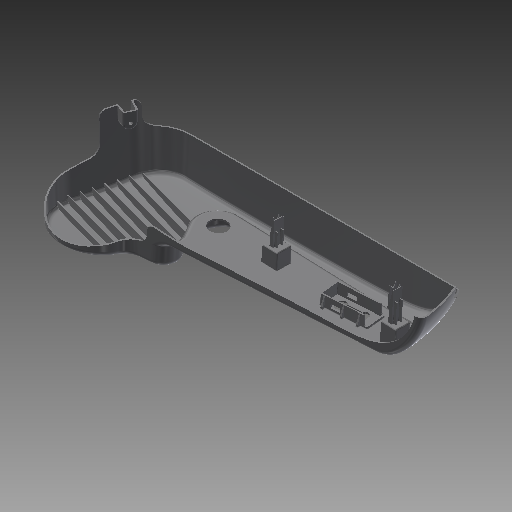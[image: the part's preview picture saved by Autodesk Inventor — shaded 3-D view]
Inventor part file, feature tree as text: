
AUTODESK INVENTOR PART (.ipt)
format: ipt  version: 2019 (Build 230136000, 136)  size: 7,566,848 bytes
history: native  units: in
note: dims shown in document units (in); Inventor stores cm internally (conversion verified against a paired STEP export)
features: other x32, fillet x25, surface_op x15, sketch x14, extrude x9, plane x8, split x7, delete_face x3, rib x3, projected_geometry x2, thicken_offset x1, draft x1, reference x1, loft x1
ambient origin geometry x8: Origin, YZ Plane, XZ Plane, XY Plane, X Axis, Y Axis, Z Axis, Center Point
bodies: Solid1 (feature_tree)
feature tree (122):
  surface_op  "Extend1"
  surface_op  "Extend2"
  surface_op  "Stitch Surface1"
  plane  "Work Plane1"
  surface_op  "Stitch Surface2"
  fillet  "Fillet1"  Radius=0.0787in
  split  "Split1"
  split  "Split2"
  split  "Split3"
  delete_face  "Delete Face1"
  plane  "Work Plane2"
  split  "Split4"
  split  "Split5"
  delete_face  "Delete Face2"
  split  "Split6"
  delete_face  "Delete Face3"
  thicken_offset  "Thicken1"
  fillet  "Fillet2"  Radius=0.0787in
  fillet  "Fillet3"  Radius=0.1969in
  extrude  "Extrusion1"  Depth=3.937in
  sketch  "Sketch6"  dims[d28=1.063in d29=9.0551in d30=0.0394in d31=0.0787in d32=0.0394in d33=0.0787in d34=0.0394in d35=-3.5433in]
  other  "iFeature3:1"
  other  "Work Point1"
  other  "Work Point2"
  other  "Work Point3"
  other  "iFeature8:2"
  fillet  "Fillet4"  Radius=0.7874in
  fillet  "Fillet5"  Radius=0.7874in
  other  "Work Point4"
  other  "Work Point5"
  other  "Work Point6"
  other  "iFeature8:3"
  fillet  "Fillet6"  [1 undecoded]
  fillet  "Fillet7"  Radius=4.9213in
  fillet  "Fillet8"  Radius=10.5in
  plane  "Work Plane3"
  other  "Work Axis1"
  sketch  "Sketch12"  dims[d47=0.0in d48=0.0in d83=0.7874in d84=0.2165in d85=0.0984in d86=0.0in d87=1.9685in d88=0.0in d89=0.0984in d98=0.0984in]
  extrude  "Extrusion4"  Depth=2.7559in
  extrude  "Extrusion5"  Depth=0.5906in
  plane  "Work Plane4"
  extrude  "Extrusion8"  [1 undecoded]
  plane  "Work Plane6"
  split  "Split8"
  draft  "FaceDraft1"
  extrude  "Extrusion9"  Depth=13.7795in
  fillet  "Fillet23"  Radius=0.0984in
  fillet  "Fillet24"  Radius=0.3937in
  fillet  "Fillet25"  Radius=0.3937in
  fillet  "Fillet26"  Radius=1.1811in
  plane  "Work Plane7"
  rib  "Rib3"
  fillet  "Fillet27"  Radius=0.3937in
  plane  "Work Plane8"
  plane  "Work Plane9"
  rib  "Rib4"
  extrude  "Extrusion10"  Depth=9.0551in
  fillet  "Fillet28"  Radius=0.0394in
  fillet  "Fillet29"  Radius=0.0787in
  fillet  "Fillet30"  Radius=0.0394in
  fillet  "Fillet31"  Radius=0.0787in
  fillet  "Fillet32"  Radius=0.0394in
  fillet  "Fillet33"  [1 undecoded]
  rib  "Rib5"
  extrude  "Extrusion11"  TaperAngle=0.0deg  [1 undecoded]
  fillet  "Fillet34"  Radius=0.7874in
  fillet  "Fillet35"  Radius=0.2165in
  fillet  "Fillet36"  Radius=0.0984in
  fillet  "Fillet37"  Radius=1.9685in
  fillet  "Fillet38"  Radius=0.0984in
  fillet  "Fillet39"  Radius=0.0984in
  other  "Srf5"
  other  "Srf6"
  other  "Edges1"
  other  "Edges2"
  other  "Srf7"
  other  "Srf8"
  sketch  "Sketch1"  dims[d3=0.7874in d4=3.937in d5=0.7874in d6=90.0deg d7=0.7874in d8=90.0deg d9=-13.7795in d10=4.9213in d11=10.5in d12=0.0in]
  other  "Srf9"
  sketch  "Sketch2"  dims[d13=0.7874in d14=2.7559in]
  other  "Srf12"
  other  "Srf13"
  sketch  "Sketch3"  dims[d15=2.5591in d16=0.5906in]
  other  "Srf14"
  sketch  "Sketch4"  dims[d17=26.5in d18=0.0in d19=-0.9843in]
  sketch  "Sketch5"  dims[d20=0.315in d21=13.7795in d22=0.0984in d23=0.3937in d24=0.3937in d25=1.1811in d26=0.3937in d27=0.0in]
  reference  "Reference1"
  other  "Srf16"
  sketch  "Sketch14"  dims[d99=0.5906in d100=1.9685in d101=0.0206in]
  sketch  "Sketch16"  dims[d102=0.0206in d103=0.2165in]
  projected_geometry  "Projected Loop1"
  sketch  "Sketch17"  dims[d104=1.9685in d105=0.0in d107=0.0591in]
  sketch  "Sketch18"  dims[d108=0.1181in]
  other  "Srf18"
  sketch  "Sketch19"  dims[d109=0.0394in]
  sketch  "Sketch20"  dims[d110=0.0787in]
  sketch  "Sketch21"  dims[d111=-5.1181in d112=75.0deg d113=3.1496in d115=0.6693in d116=0.3937in d118=0.3937in d120=0.0591in d121=0.0394in d122=0.0034in d123=0.0197in d124=0.8268in d125=0.1181in d126=0.1181in d127=0.5118in d128=0.2362in d129=0.2362in d130=0.2362in d131=0.2362in d132=1.9685in d133=0.0394in d134=0.0394in d135=0.0069in d136=0.0in d137=0.0in d138=0.0079in d139=0.1374in d140=0.1374in d141=0.5906in d142=1.0in d143=0.0in d144=0.0394in d145=0.0394in d146=0.0394in d147=0.0394in d148=0.0197in d149=0.0197in d150=1.1024in d151=0.5118in d152=0.1181in d153=0.1181in d154=0.2362in d155=0.2362in d156=0.2362in d157=0.2362in d158=9.8425in d159=0.0394in d160=0.0394in d161=0.0069in d162=0.1374in d163=0.1374in d164=0.0079in d165=0.5906in d166=8.75in d167=0.0in d168=0.0394in d169=0.0394in d170=0.0394in d171=0.0394in d172=0.0197in d173=0.0197in d174=0.01in d175=0.01in]
  surface_op  "Surface1"
  surface_op  "Surface2"
  surface_op  "Surface3"
  surface_op  "Surface4"
  other  "OffsetSrf1"
  other  "OffsetSrf2"
  extrude  "ExtrusionSrf1"  Depth=1.9685in
  surface_op  "Surface5"
  extrude  "ExtrusionSrf2"  Depth=0.2165in
  surface_op  "Surface7"
  surface_op  "Boundary Patch2"
  surface_op  "Surface8"
  surface_op  "Boundary Patch3"
  other  "Srf1"
  other  "Srf2"
  other  "Srf3"
  other  "Srf4"
  loft  "LoftSrf1"
  other  "Srf10"
  surface_op  "Surface6"
  other  "Srf11"
  surface_op  "Boundary Patch1"
  other  "Srf15"
  other  "Srf17"
  projected_geometry  "Project Cut Edges1"
note: 4 required parameter values undecoded (feature->parameter linkage not recoverable at this tier; creation-order binding heuristic only, values carry confidence <= 0.55)
